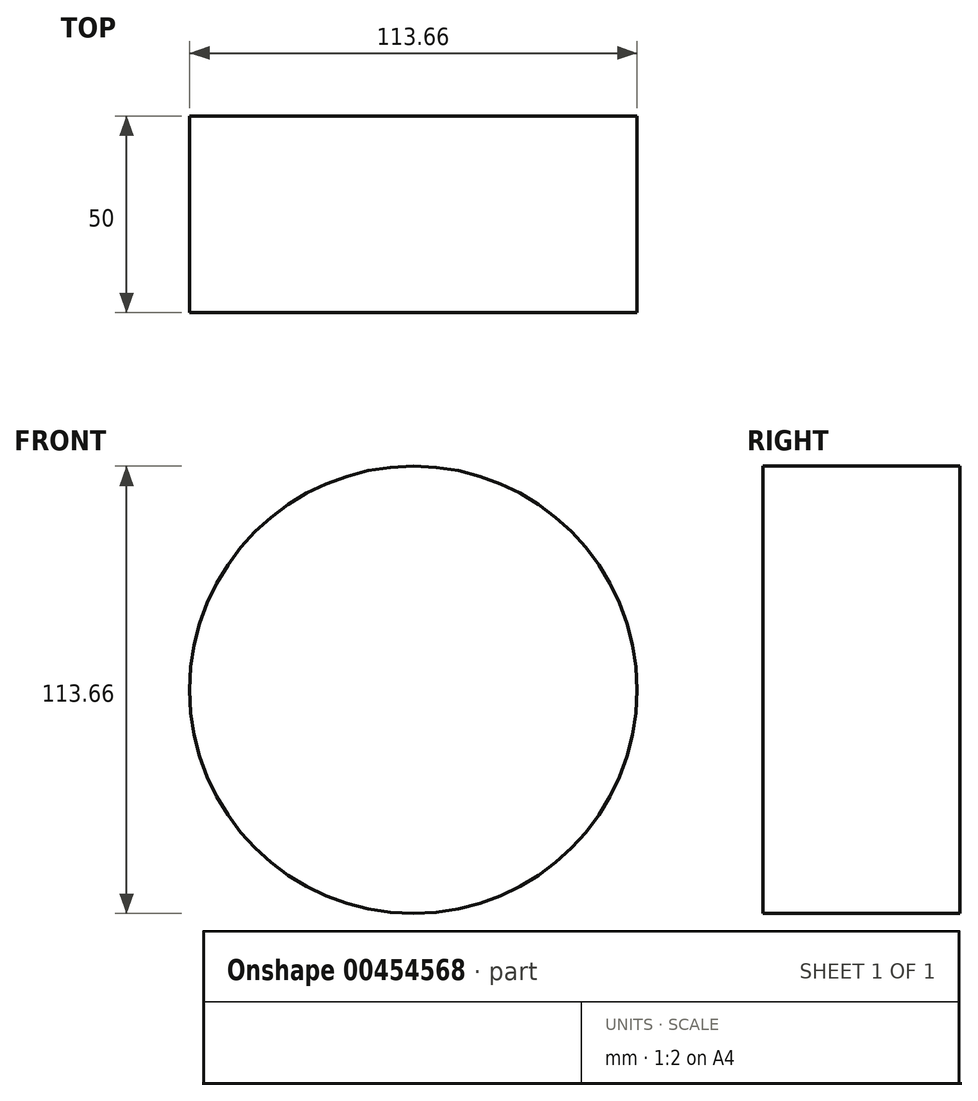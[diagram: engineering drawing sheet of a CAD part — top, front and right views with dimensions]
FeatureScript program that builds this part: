
annotation { "Feature Type Name" : "Feature", "Feature Type Description" : "" }
export const myFeature = defineFeature(function(context is Context, id is Id, definition is map)
    precondition{}
    {
        {
            var Q0;
            Q0=qCreatedBy(makeId("Front.planeOp"),FACE);
            var sketch = newSketch(context, id + "F0", { "sketchPlane" : qUnion([Q0])});
            skCircle(sketch, "E0", {"center": v(0, 0) * mm, "radius": 56.83 * mm});
            skSolve(sketch);
        }
        {
            var Q0;
            Q0 = qSketchRegion(id + "F0", true);
            var Q1;
            Q1=sQuery(id+"F0.wireOp",EDGE,"E0");
            extrude(context, id + "F1", {"bodyType" : ToolBodyType.SURFACE, "surfaceEntities" : qUnion([Q0, Q1]), "depth" : 50 * mm});
        }
    });
